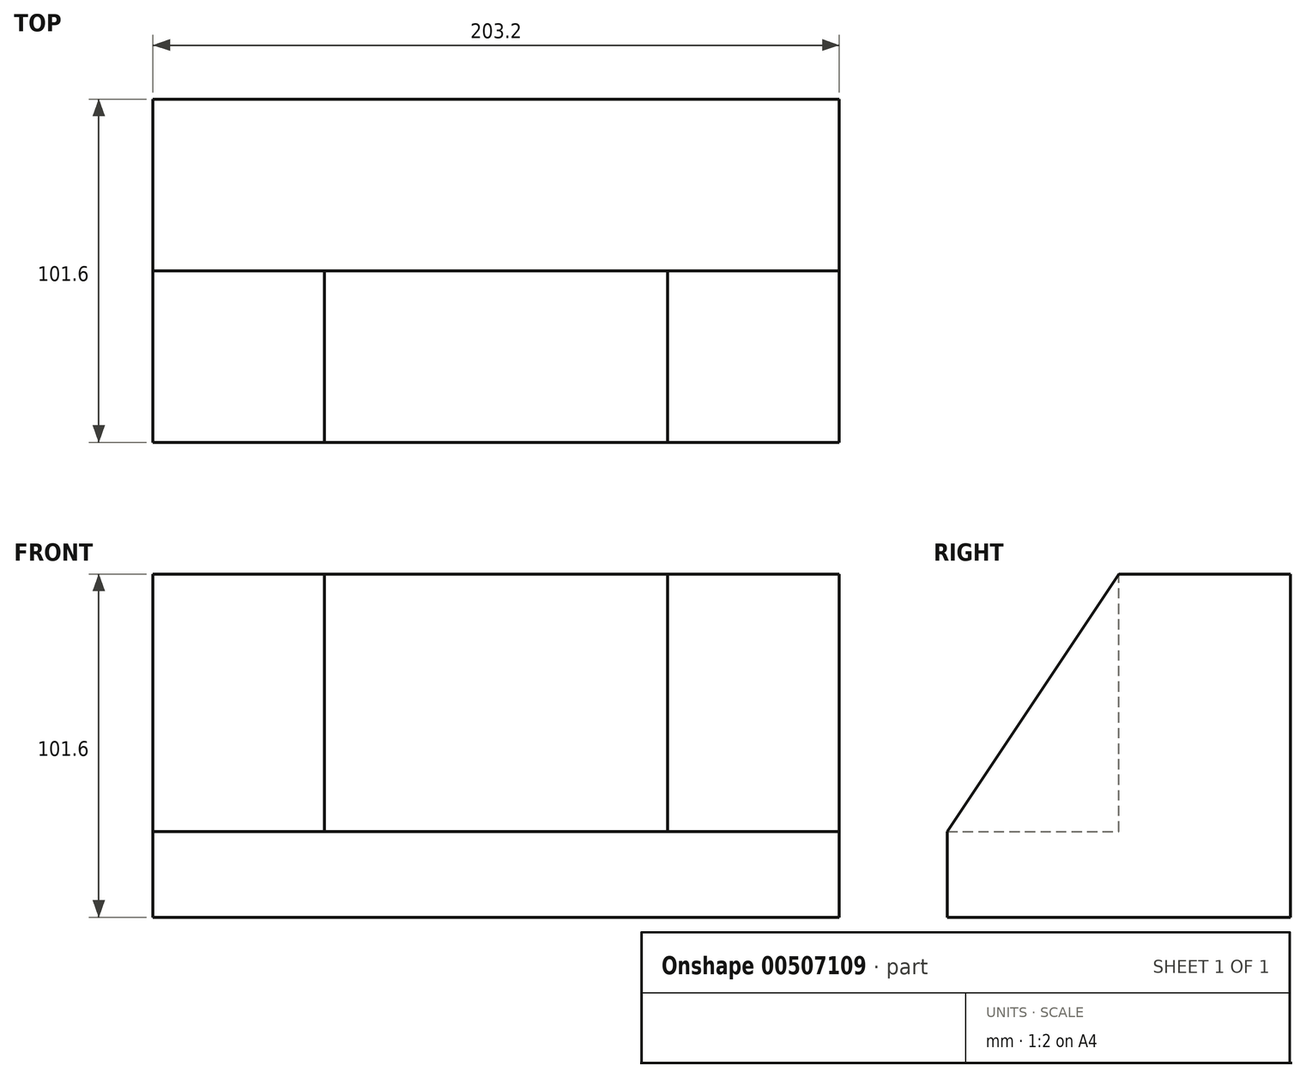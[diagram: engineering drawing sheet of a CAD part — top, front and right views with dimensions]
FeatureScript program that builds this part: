
annotation { "Feature Type Name" : "Feature", "Feature Type Description" : "" }
export const myFeature = defineFeature(function(context is Context, id is Id, definition is map)
    precondition{}
    {
        {
            var Q0;
            Q0=qCreatedBy(makeId("Right.planeOp"),FACE);
            var sketch = newSketch(context, id + "F0", { "sketchPlane" : qUnion([Q0])});
            skLineSegment(sketch, "E0", {"start": v(0, 0) * mm, "end": v(0, 25.4) * mm});
            skLineSegment(sketch, "E1", {"start": v(0, 0) * mm, "end": v(101.6, 0) * mm});
            skLineSegment(sketch, "E2", {"start": v(101.6, 0) * mm, "end": v(101.6, 101.6) * mm});
            skLineSegment(sketch, "E3", {"start": v(101.6, 101.6) * mm, "end": v(50.8, 101.6) * mm});
            skLineSegment(sketch, "E4", {"start": v(50.8, 101.6) * mm, "end": v(0, 25.4) * mm});
            skSolve(sketch);
        }
        {
            var Q0;
            Q0=makeQuery(id+"F0.imprint","IMPRINT",FACE,{"disambiguationData":[TD([[makeQuery(id+"F0.imprint","IMPRINT",EDGE,{"derivedFrom":sQuery(id+"F0.wireOp",EDGE,"E0")}),-1.0]])]});
            extrude(context, id + "F1", {"entities" : qUnion([Q0]), "oppositeDirection" : true, "depth" : 50.8 * mm});
        }
        {
            var Q0;
            Q0=makeQuery(id+"F1.opExtrude","CAP_FACE",FACE,{"disambiguationData":[OSD([sQuery(id+"F0.wireOp",EDGE,"E0"),sQuery(id+"F0.wireOp",EDGE,"E1"),sQuery(id+"F0.wireOp",EDGE,"E2"),sQuery(id+"F0.wireOp",EDGE,"E3"),sQuery(id+"F0.wireOp",EDGE,"E4")])],"isStart":false});
            var sketch = newSketch(context, id + "F2", { "sketchPlane" : qUnion([Q0])});
            skLineSegment(sketch, "E5", {"start": v(0, 25.4) * mm, "end": v(-50.8, 25.4) * mm});
            skLineSegment(sketch, "E6", {"start": v(-50.8, 25.4) * mm, "end": v(-50.8, 101.6) * mm});
            skLineSegment(sketch, "E7", {"start": v(-50.8, 101.6) * mm, "end": v(-101.6, 101.6) * mm});
            skLineSegment(sketch, "E8", {"start": v(-101.6, 101.6) * mm, "end": v(-101.6, 0) * mm});
            skLineSegment(sketch, "E9", {"start": v(-101.6, 0) * mm, "end": v(0, 0) * mm});
            skLineSegment(sketch, "E10", {"start": v(0, 0) * mm, "end": v(0, 25.4) * mm});
            skSolve(sketch);
        }
        {
            var Q0;
            Q0=makeQuery(id+"F2.imprint","IMPRINT",FACE,{"disambiguationData":[TD([[makeQuery(id+"F2.imprint","IMPRINT",EDGE,{"derivedFrom":sQuery(id+"F2.wireOp",EDGE,"E5")}),1.0]])]});
            extrude(context, id + "F3", {"entities" : qUnion([Q0]), "operationType" : NewBodyOperationType.ADD, "depth" : 101.6 * mm});
        }
        {
            var Q0;
            Q0=makeQuery(id+"F3.opExtrude","CAP_FACE",FACE,{"disambiguationData":[OSD([sQuery(id+"F2.wireOp",EDGE,"E5"),sQuery(id+"F2.wireOp",EDGE,"E6"),sQuery(id+"F2.wireOp",EDGE,"E7"),sQuery(id+"F2.wireOp",EDGE,"E8"),sQuery(id+"F2.wireOp",EDGE,"E9"),sQuery(id+"F2.wireOp",EDGE,"E10")])],"isStart":false});
            var sketch = newSketch(context, id + "F4", { "sketchPlane" : qUnion([Q0])});
            skLineSegment(sketch, "E11", {"start": v(-101.6, 101.6) * mm, "end": v(-50.8, 101.6) * mm});
            skLineSegment(sketch, "E12", {"start": v(-50.8, 101.6) * mm, "end": v(0, 25.4) * mm});
            skLineSegment(sketch, "E13", {"start": v(0, 25.4) * mm, "end": v(0, 0) * mm});
            skLineSegment(sketch, "E14", {"start": v(0, 0) * mm, "end": v(-101.6, 0) * mm});
            skLineSegment(sketch, "E15", {"start": v(-101.6, 0) * mm, "end": v(-101.6, 101.6) * mm});
            skSolve(sketch);
        }
        {
            var Q0;
            Q0=makeQuery(id+"F4.imprint","IMPRINT",FACE,{"disambiguationData":[TD([[makeQuery(id+"F4.imprint","IMPRINT",EDGE,{"derivedFrom":sQuery(id+"F4.wireOp",EDGE,"E12")}),-1.0]])]});
            var Q1;
            Q1=makeQuery(id+"F4.imprint","IMPRINT",FACE,{"disambiguationData":[TD([[makeQuery(id+"F4.imprint","IMPRINT",EDGE,{"derivedFrom":sQuery(id+"F4.wireOp",EDGE,"E11")}),-1.0]])]});
            extrude(context, id + "F5", {"entities" : qUnion([Q0, Q1]), "operationType" : NewBodyOperationType.ADD, "depth" : 50.8 * mm});
        }
    });
